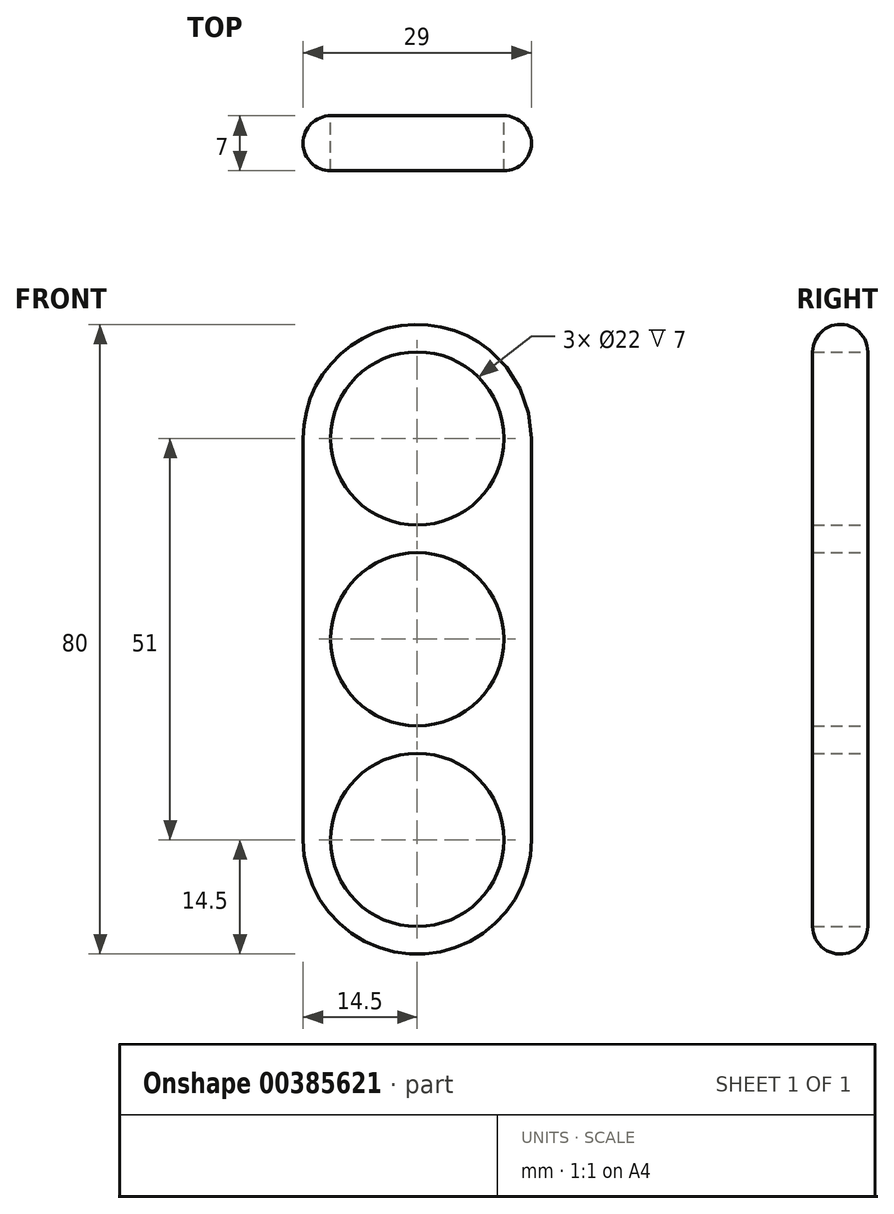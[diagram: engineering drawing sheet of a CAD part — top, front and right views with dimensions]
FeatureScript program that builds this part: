
annotation { "Feature Type Name" : "Feature", "Feature Type Description" : "" }
export const myFeature = defineFeature(function(context is Context, id is Id, definition is map)
    precondition{}
    {
        {
            var Q0;
            Q0=qCreatedBy(makeId("Front.planeOp"),FACE);
            var sketch = newSketch(context, id + "F0", { "sketchPlane" : qUnion([Q0])});
            skCircle(sketch, "E0", {"center": v(0, 0) * mm, "radius": 11 * mm});
            skArc(sketch, "E1", {"start": v(14.5, 25.5) * mm, "mid": v(0, 40) * mm, "end": v(-14.5, 25.5) * mm});
            skCircle(sketch, "E2", {"center": v(0, 25.5) * mm, "radius": 11 * mm});
            skLineSegment(sketch, "E3", {"start": v(-14.5, 25.5) * mm, "end": v(-14.5, 0) * mm});
            skLineSegment(sketch, "E4", {"start": v(14.5, 25.5) * mm, "end": v(14.5, 0) * mm});
            skCircle(sketch, "E5.1.0", {"center": v(0, -25.5) * mm, "radius": 11 * mm});
            skArc(sketch, "E5.1.1", {"start": v(-14.5, -25.5) * mm, "mid": v(0, -40) * mm, "end": v(14.5, -25.5) * mm});
            skLineSegment(sketch, "E5.1.2", {"start": v(14.5, -25.5) * mm, "end": v(14.5, 0) * mm});
            skLineSegment(sketch, "E5.1.3", {"start": v(-14.5, -25.5) * mm, "end": v(-14.5, 0) * mm});
            skSolve(sketch);
        }
        {
            var Q0;
            Q0=makeQuery(id+"F0.imprint","IMPRINT",FACE,{"disambiguationData":[TD([[makeQuery(id+"F0.imprint","IMPRINT",EDGE,{"derivedFrom":sQuery(id+"F0.wireOp",EDGE,"E0")}),-1.0]])]});
            extrude(context, id + "F1", {"entities" : qUnion([Q0]), "depth" : 7 * mm, "offsetDistance" : 25 * mm});
        }
        {
            var Q0;
            Q0=makeQuery(id+"F1.opExtrude","CAP_EDGE",EDGE,{"disambiguationData":[OSD([sQuery(id+"F0.wireOp",EDGE,"E1")])],"isStart":false});
            var Q1;
            Q1=makeQuery(id+"F1.opExtrude","CAP_EDGE",EDGE,{"disambiguationData":[OSD([sQuery(id+"F0.wireOp",EDGE,"E1")])],"isStart":true});
            fillet(context, id + "F2", {"entities" : qUnion([Q0, Q1]), "radius" : 3.5 * mm, "tangentPropagation" : true, "allowEdgeOverflow" : false});
        }
    });
